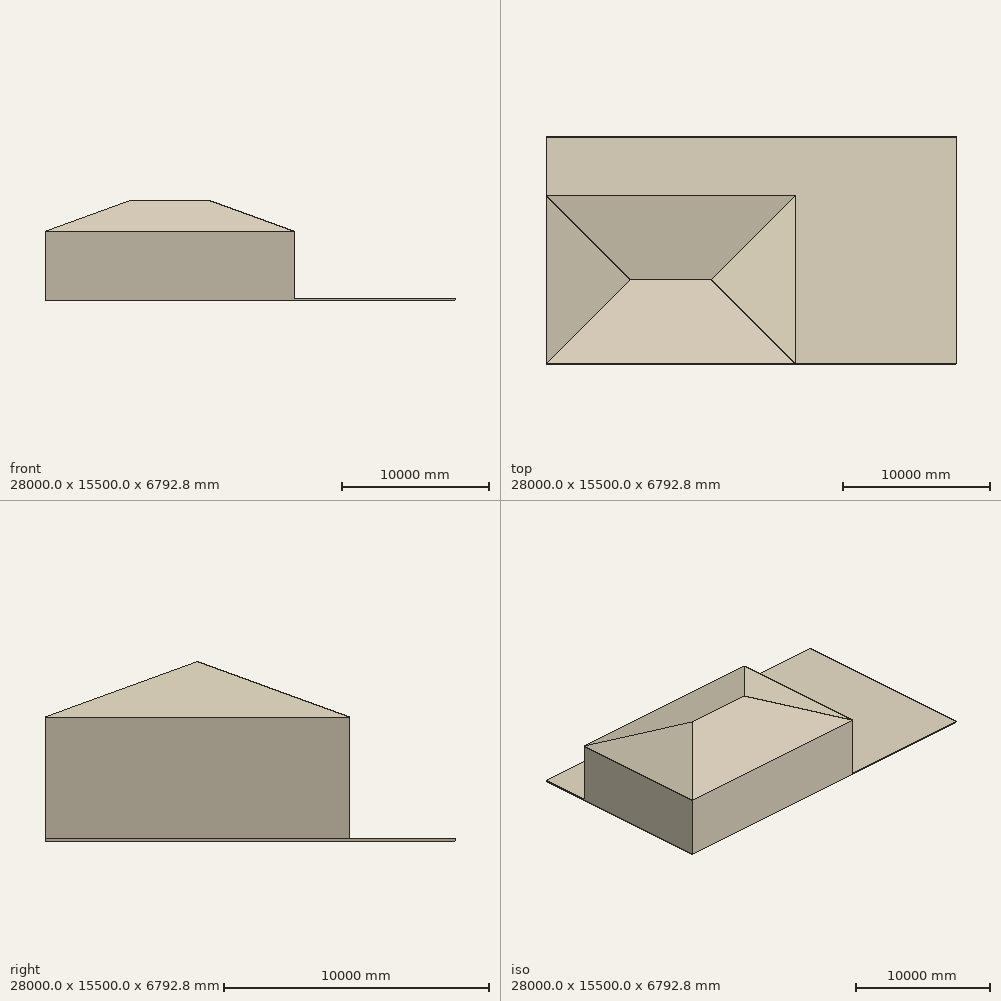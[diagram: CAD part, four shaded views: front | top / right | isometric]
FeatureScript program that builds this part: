
annotation { "Feature Type Name" : "Feature", "Feature Type Description" : "" }
export const myFeature = defineFeature(function(context is Context, id is Id, definition is map)
    precondition{}
    {
        {
            var Q0;
            Q0=qCreatedBy(makeId("Top.planeOp"),FACE);
            var sketch = newSketch(context, id + "F0", { "sketchPlane" : qUnion([Q0])});
            skLineSegment(sketch, "E0.bottom", {"start": v(0, 0) * mm, "end": v(-28000, 0) * mm});
            skLineSegment(sketch, "E0.top", {"start": v(0, -15500) * mm, "end": v(-28000, -15500) * mm});
            skLineSegment(sketch, "E0.left", {"start": v(0, 0) * mm, "end": v(0, -15500) * mm});
            skLineSegment(sketch, "E0.right", {"start": v(-28000, 0) * mm, "end": v(-28000, -15500) * mm});
            skSolve(sketch);
        }
        {
            var Q0;
            Q0=qSketchRegion(id+"F0",true);
            extrude(context, id + "F1", {"entities" : qUnion([Q0]), "oppositeDirection" : true, "depth" : 100 * mm});
        }
        {
            var Q0;
            Q0=makeQuery(id+"F1.opExtrude","CAP_FACE",FACE,{"disambiguationData":[OSD([sQuery(id+"F0.wireOp",EDGE,"E0.bottom"),sQuery(id+"F0.wireOp",EDGE,"E0.top"),sQuery(id+"F0.wireOp",EDGE,"E0.left"),sQuery(id+"F0.wireOp",EDGE,"E0.right")])],"isStart":true});
            var sketch = newSketch(context, id + "F2", { "sketchPlane" : qUnion([Q0])});
            skLineSegment(sketch, "E1.bottom", {"start": v(-28000, -15500) * mm, "end": v(-11000, -15500) * mm});
            skLineSegment(sketch, "E1.top", {"start": v(-28000, -4000) * mm, "end": v(-11000, -4000) * mm});
            skLineSegment(sketch, "E1.left", {"start": v(-28000, -15500) * mm, "end": v(-28000, -4000) * mm});
            skLineSegment(sketch, "E1.right", {"start": v(-11000, -15500) * mm, "end": v(-11000, -4000) * mm});
            skSolve(sketch);
        }
        {
            var Q0;
            Q0=makeQuery(id+"F2.imprint","IMPRINT",FACE,{"disambiguationData":[TD([[makeQuery(id+"F2.imprint","IMPRINT",EDGE,{"derivedFrom":sQuery(id+"F2.wireOp",EDGE,"E1.bottom")}),-1.0]])]});
            extrude(context, id + "F3", {"entities" : qUnion([Q0]), "operationType" : NewBodyOperationType.ADD, "depth" : 4600 * mm});
        }
        {
            var Q0;
            Q0=makeQuery(id+"F3.boolean.opBoolean","MERGE",FACE,{"derivedFrom":[makeQuery(id+"F1.opExtrude","SWEPT_FACE",FACE,{"disambiguationData":[OSD([sQuery(id+"F0.wireOp",EDGE,"E0.right")])]}),makeQuery(id+"F3.opExtrude","SWEPT_FACE",FACE,{"disambiguationData":[OSD([sQuery(id+"F2.wireOp",EDGE,"E1.left")])]})]});
            var sketch = newSketch(context, id + "F4", { "sketchPlane" : qUnion([Q0])});
            skLineSegment(sketch, "E2.0", {"start": v(4000, 4600) * mm, "end": v(15500, 4600) * mm});
            skLineSegment(sketch, "E3", {"start": v(4000, 4600) * mm, "end": v(9750, 6692.83) * mm});
            skLineSegment(sketch, "E4", {"start": v(9750, 6692.83) * mm, "end": v(15500, 4600) * mm});
            skSolve(sketch);
        }
        {
            var Q0;
            Q0=qSketchRegion(id+"F4",true);
            var Q1;
            Q1=makeQuery(id+"F3.opExtrude","SWEPT_FACE",FACE,{"disambiguationData":[OSD([sQuery(id+"F2.wireOp",EDGE,"E1.right")])]});
            extrude(context, id + "F5", {"entities" : qUnion([Q0]), "operationType" : NewBodyOperationType.ADD, "endBound" : BoundingType.UP_TO_SURFACE, "oppositeDirection" : true, "endBoundEntityFace" : qUnion([Q1]), "depth" : 25 * mm});
        }
        {
            var Q0;
            Q0=makeQuery(id+"F3.opExtrude","SWEPT_FACE",FACE,{"disambiguationData":[OSD([sQuery(id+"F2.wireOp",EDGE,"E1.top")])]});
            var sketch = newSketch(context, id + "F6", { "sketchPlane" : qUnion([Q0])});
            skLineSegment(sketch, "E5.0", {"start": v(11000, 6692.83) * mm, "end": v(11000, 4600) * mm});
            skLineSegment(sketch, "E5.1", {"start": v(28000, 4600) * mm, "end": v(28000, 6692.83) * mm});
            skLineSegment(sketch, "E5.2", {"start": v(11000, 6692.83) * mm, "end": v(28000, 6692.83) * mm});
            skLineSegment(sketch, "E6", {"start": v(11000, 4600) * mm, "end": v(16750, 6692.83) * mm});
            skLineSegment(sketch, "E7", {"start": v(28000, 4600) * mm, "end": v(22250, 6692.83) * mm});
            skSolve(sketch);
        }
        {
            var Q0;
            Q0=qSketchRegion(id+"F6",true);
            extrude(context, id + "F7", {"entities" : qUnion([Q0]), "operationType" : NewBodyOperationType.REMOVE, "endBound" : BoundingType.THROUGH_ALL, "oppositeDirection" : true, "depth" : 25 * mm});
        }
    });
